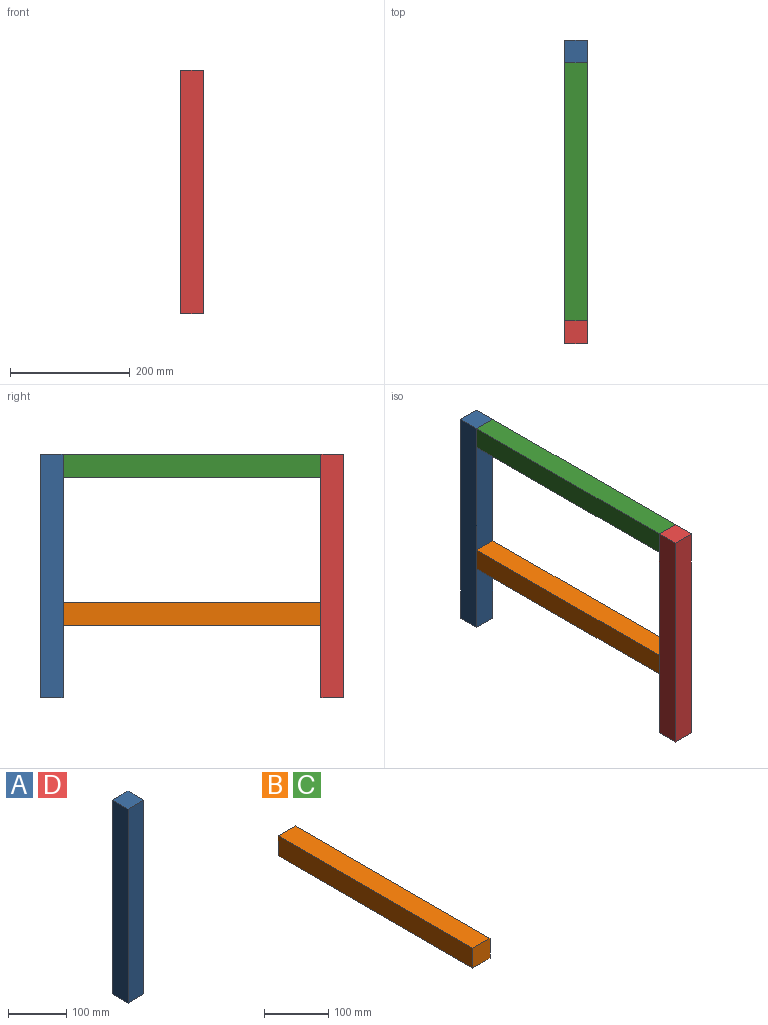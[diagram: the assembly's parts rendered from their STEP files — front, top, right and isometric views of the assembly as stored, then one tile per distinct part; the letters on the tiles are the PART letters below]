
ASSEMBLY  parts=4 mates=3
PART A: 6 faces, bbox 38x38x406 mm
  f0: plane 38x38mm, normal (0,0,1), area 1444mm2, adj f1,f3,f4,f5
  f1: plane 406x38mm, normal (-1,0,0), area 15428mm2, adj f0,f2,f4,f5
  f2: plane 38x38mm, normal (0,0,-1), area 1444mm2, adj f1,f3,f4,f5
  f3: plane 406x38mm, normal (1,0,0), area 15428mm2, adj f0,f2,f4,f5
  f4: plane 406x38mm, normal (0,-1,0), area 15428mm2, adj f0,f1,f2,f3
  f5: plane 406x38mm, normal (0,1,0), area 15428mm2, adj f0,f1,f2,f3
PART B: 6 faces, bbox 38x430x38 mm
  f0: plane 430x38mm, normal (0,0,1), area 16340mm2, adj f1,f3,f4,f5
  f1: plane 38x38mm, normal (0,-1,0), area 1444mm2, adj f0,f2,f4,f5
  f2: plane 430x38mm, normal (0,0,-1), area 16340mm2, adj f1,f3,f4,f5
  f3: plane 38x38mm, normal (0,1,0), area 1444mm2, adj f0,f2,f4,f5
  f4: plane 430x38mm, normal (1,0,0), area 16340mm2, adj f0,f1,f2,f3
  f5: plane 430x38mm, normal (-1,0,0), area 16340mm2, adj f0,f1,f2,f3
PART C: same geometry as B
PART D: same geometry as A
PLACE A t=(-259.94,499.5,-92.03)mm
PLACE B t=(-297.94,461.5,27.97)mm
PLACE C t=(-297.94,461.5,275.97)mm
PLACE D t=(-259.94,31.5,-92.03)mm
MATE fastened C.f3 <-> A.f4  axis (0,1,0) through (-278.94,461.5,313.97)mm
MATE fastened D.f5 <-> B.f1  axis (0,1,0) through (-278.94,31.5,-92.03)mm
MATE fastened C.f1 <-> D.f5  axis (0,-1,0) through (-278.94,31.5,313.97)mm
